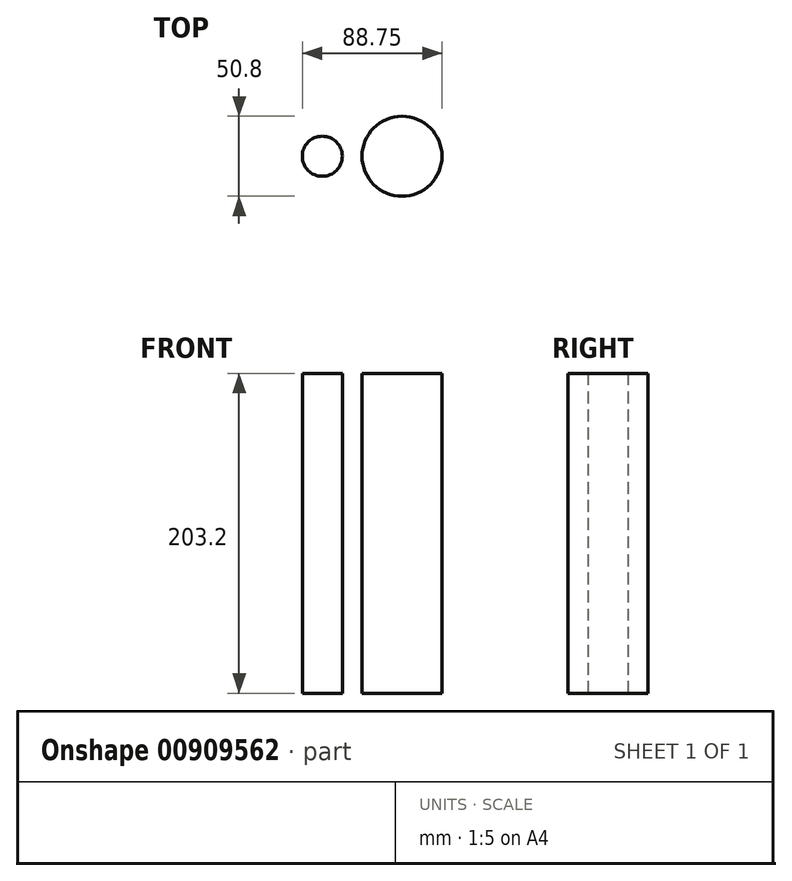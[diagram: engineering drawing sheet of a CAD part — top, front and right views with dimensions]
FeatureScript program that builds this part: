
annotation { "Feature Type Name" : "Feature", "Feature Type Description" : "" }
export const myFeature = defineFeature(function(context is Context, id is Id, definition is map)
    precondition{}
    {
        {
            var Q0;
            Q0=qCreatedBy(makeId("Top.planeOp"),FACE);
            var sketch = newSketch(context, id + "F0", { "sketchPlane" : qUnion([Q0])});
            skCircle(sketch, "E0", {"center": v(0, 0) * mm, "radius": 25.4 * mm});
            skCircle(sketch, "E1", {"center": v(-50.65, 0) * mm, "radius": 12.7 * mm});
            skSolve(sketch);
        }
        {
            var Q0;
            Q0=qSketchRegion(id+"F0",true);
            extrude(context, id + "F1", {"entities" : qUnion([Q0]), "depth" : 203.2 * mm, "offsetDistance" : 25 * mm});
        }
    });
